# Revit family: TECHOLED BX2 SERIES LIGHTING FIXTURE
name_source: partatom
category: Lighting Fixtures
units: mm (PartAtom-declared; Revit-internal decimal feet)

## family parameters
Always vertical = Yes
Cut with Voids When Loaded = No
Light Source = Yes
OmniClass Number = 23.80.70.00
OmniClass Title = Lighting
Part Type = Normal
Room Calculation Point = No
Round Connector Dimension = Use Diameter
Shared = No
Work Plane-Based = No

## types (1)
- TechoLED-BX-2-D-4-31-30-U-D
    A = 0' - 2 3/4"
    Apparent Load = 18 VA
    B = 0' - 2 3/16"
    C = 4' - 0"
    Color Filter = 16777215
    Dimming Lamp Color Temperature Shift = <None>
    Emit Shape Visible in Rendering = No
    Emit from Rectangle Length = 4' - 0"
    Emit from Rectangle Width = 0' - 2 3/16"
    Lamp = Samsung LED Chips
    Light Source Symbol Size = 0' - 0 1/2"
    Manufacturer = TechoLED
    Model = TechoLED-BX-2-D-4-18-35-U-W-P-D
    String Length = 2' - 0"
    Type Comments = TechoLED-BX2
    Wattage Comments = 18W

## geometry (parser evidence)
native form markers: Sweep x2
no freeform markers — native parametric forms only
